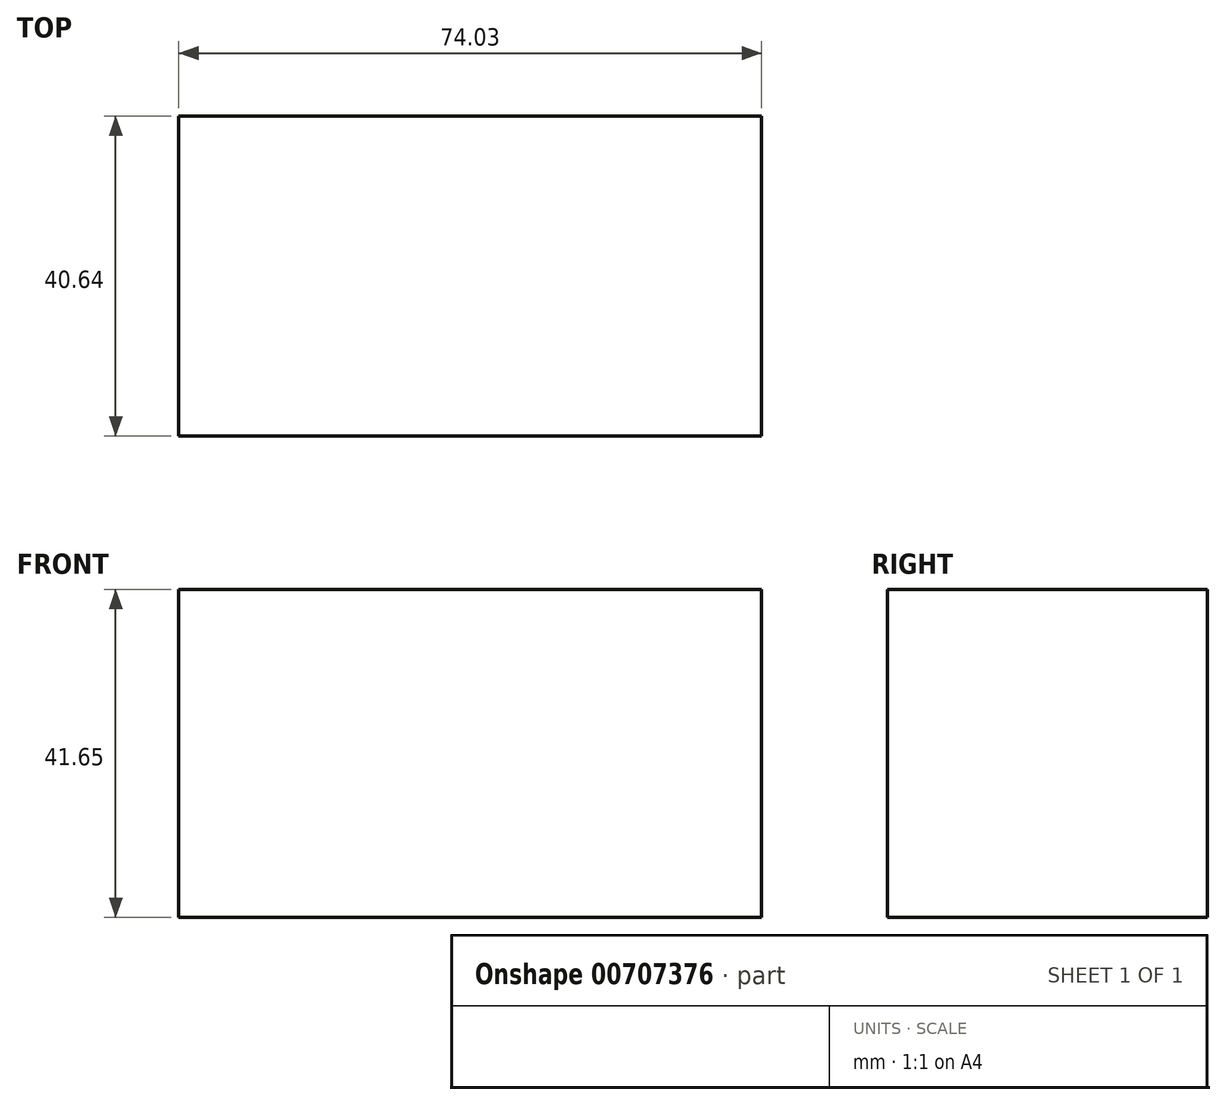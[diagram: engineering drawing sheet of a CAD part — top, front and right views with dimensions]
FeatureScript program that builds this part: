
annotation { "Feature Type Name" : "Feature", "Feature Type Description" : "" }
export const myFeature = defineFeature(function(context is Context, id is Id, definition is map)
    precondition{}
    {
        {
            var Q0;
            Q0=qCreatedBy(makeId("Front.planeOp"),FACE);
            var sketch = newSketch(context, id + "F0", { "sketchPlane" : qUnion([Q0])});
            skLineSegment(sketch, "E0.bottom", {"start": v(0, 0) * mm, "end": v(74.03, 0) * mm});
            skLineSegment(sketch, "E0.top", {"start": v(0, 41.65) * mm, "end": v(74.03, 41.65) * mm});
            skLineSegment(sketch, "E0.left", {"start": v(0, 0) * mm, "end": v(0, 41.65) * mm});
            skLineSegment(sketch, "E0.right", {"start": v(74.03, 0) * mm, "end": v(74.03, 41.65) * mm});
            skSolve(sketch);
        }
        {
            var Q0;
            Q0=makeQuery(id+"F0.imprint","IMPRINT",FACE,{"disambiguationData":[TD([[makeQuery(id+"F0.imprint","IMPRINT",EDGE,{"derivedFrom":sQuery(id+"F0.wireOp",EDGE,"E0.bottom")}),1.0]])]});
            var Q1;
            Q1=sQuery(id+"F0.wireOp",EDGE,"E0.top");
            var Q2;
            Q2=sQuery(id+"F0.wireOp",EDGE,"E0.left");
            var Q3;
            Q3=sQuery(id+"F0.wireOp",EDGE,"E0.bottom");
            var Q4;
            Q4=sQuery(id+"F0.wireOp",EDGE,"E0.right");
            extrude(context, id + "F1", {"entities" : qUnion([Q0]), "surfaceEntities" : qUnion([Q1, Q2, Q3, Q4]), "depth" : 40.64 * mm, "offsetDistance" : 25.4 * mm});
        }
    });
